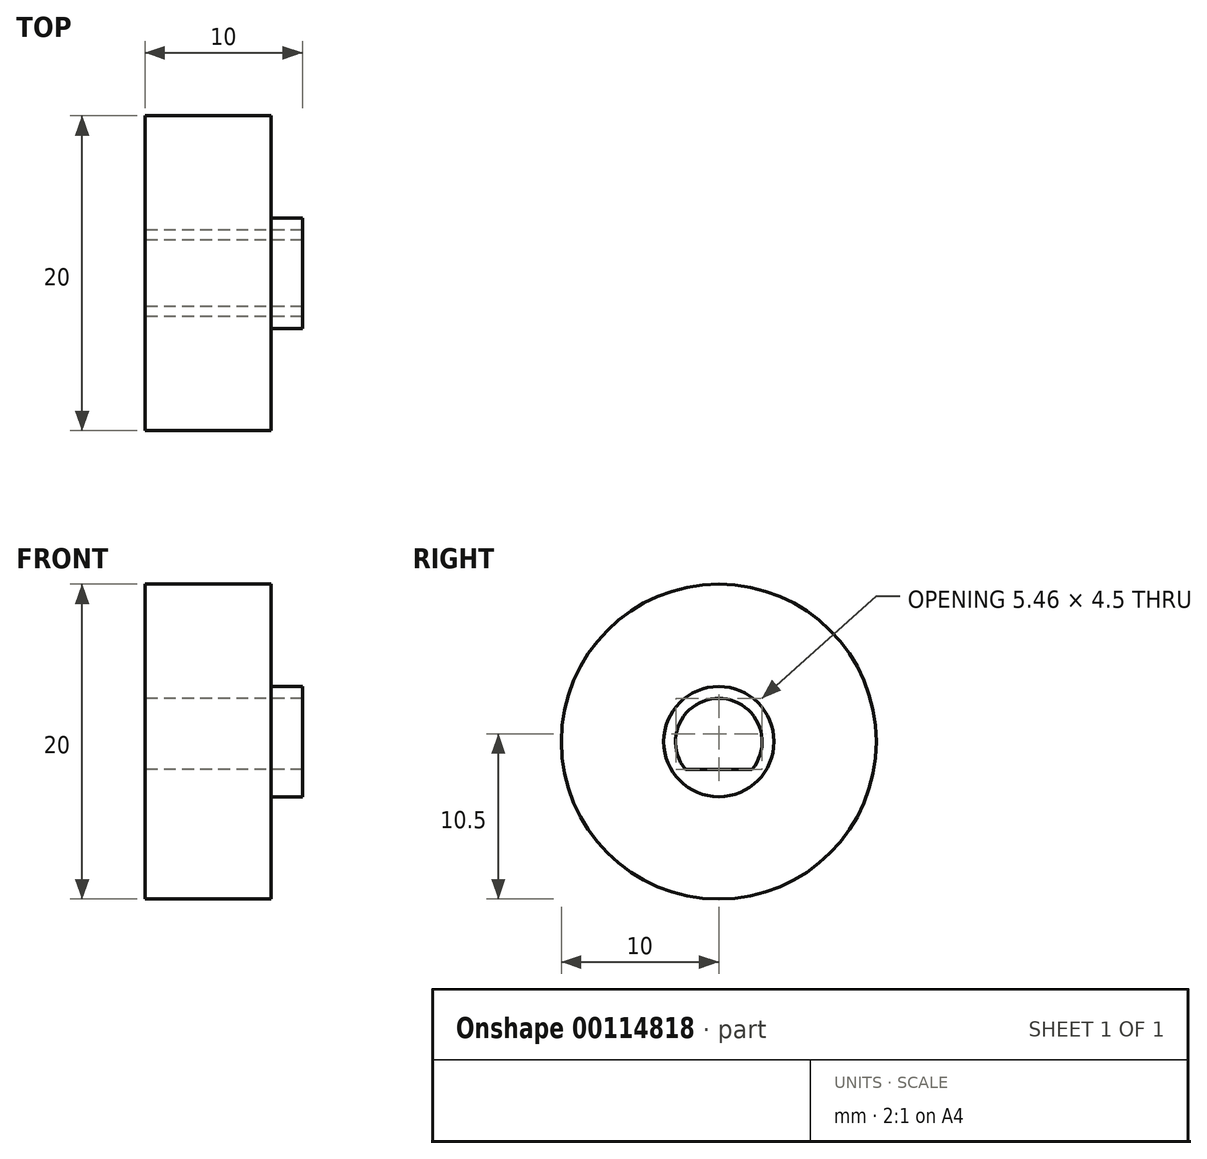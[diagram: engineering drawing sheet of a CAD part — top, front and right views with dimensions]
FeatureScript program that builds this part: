
annotation { "Feature Type Name" : "Feature", "Feature Type Description" : "" }
export const myFeature = defineFeature(function(context is Context, id is Id, definition is map)
    precondition{}
    {
        {
            var Q0;
            Q0=qCreatedBy(makeId("Right.planeOp"),FACE);
            var sketch = newSketch(context, id + "F0", { "sketchPlane" : qUnion([Q0])});
            skCircle(sketch, "E0", {"center": v(0, 0) * mm, "radius": 10 * mm});
            skArc(sketch, "E1", {"start": v(2.12, -1.75) * mm, "mid": v(0, 2.75) * mm, "end": v(-2.12, -1.75) * mm});
            skLineSegment(sketch, "E2", {"start": v(2.12, -1.75) * mm, "end": v(-2.12, -1.75) * mm});
            skSolve(sketch);
        }
        {
            var Q0;
            Q0 = qSketchRegion(id + "F0", true);
            extrude(context, id + "F1", {"entities" : qUnion([Q0]), "depth" : 10 * mm});
        }
        {
            var Q0;
            Q0=makeQuery(id+"F1.opExtrude","CAP_FACE",FACE,{"disambiguationData":[OSD([sQuery(id+"F0.wireOp",EDGE,"E0"),sQuery(id+"F0.wireOp",EDGE,"E1"),sQuery(id+"F0.wireOp",EDGE,"E2")])],"isStart":false});
            var sketch = newSketch(context, id + "F2", { "sketchPlane" : qUnion([Q0])});
            skCircle(sketch, "E3", {"center": v(0, 0) * mm, "radius": 3.5 * mm});
            skSolve(sketch);
        }
        {
            var Q0;
            Q0=makeQuery(id+"F2.imprint","IMPRINT",FACE,{"disambiguationData":[TD([[makeQuery(id+"F2.imprint","IMPRINT",EDGE,{"derivedFrom":sQuery(id+"F2.wireOp",EDGE,"E3")}),-1.0]])]});
            extrude(context, id + "F3", {"entities" : qUnion([Q0]), "operationType" : NewBodyOperationType.REMOVE, "oppositeDirection" : true, "depth" : 2 * mm});
        }
    });
